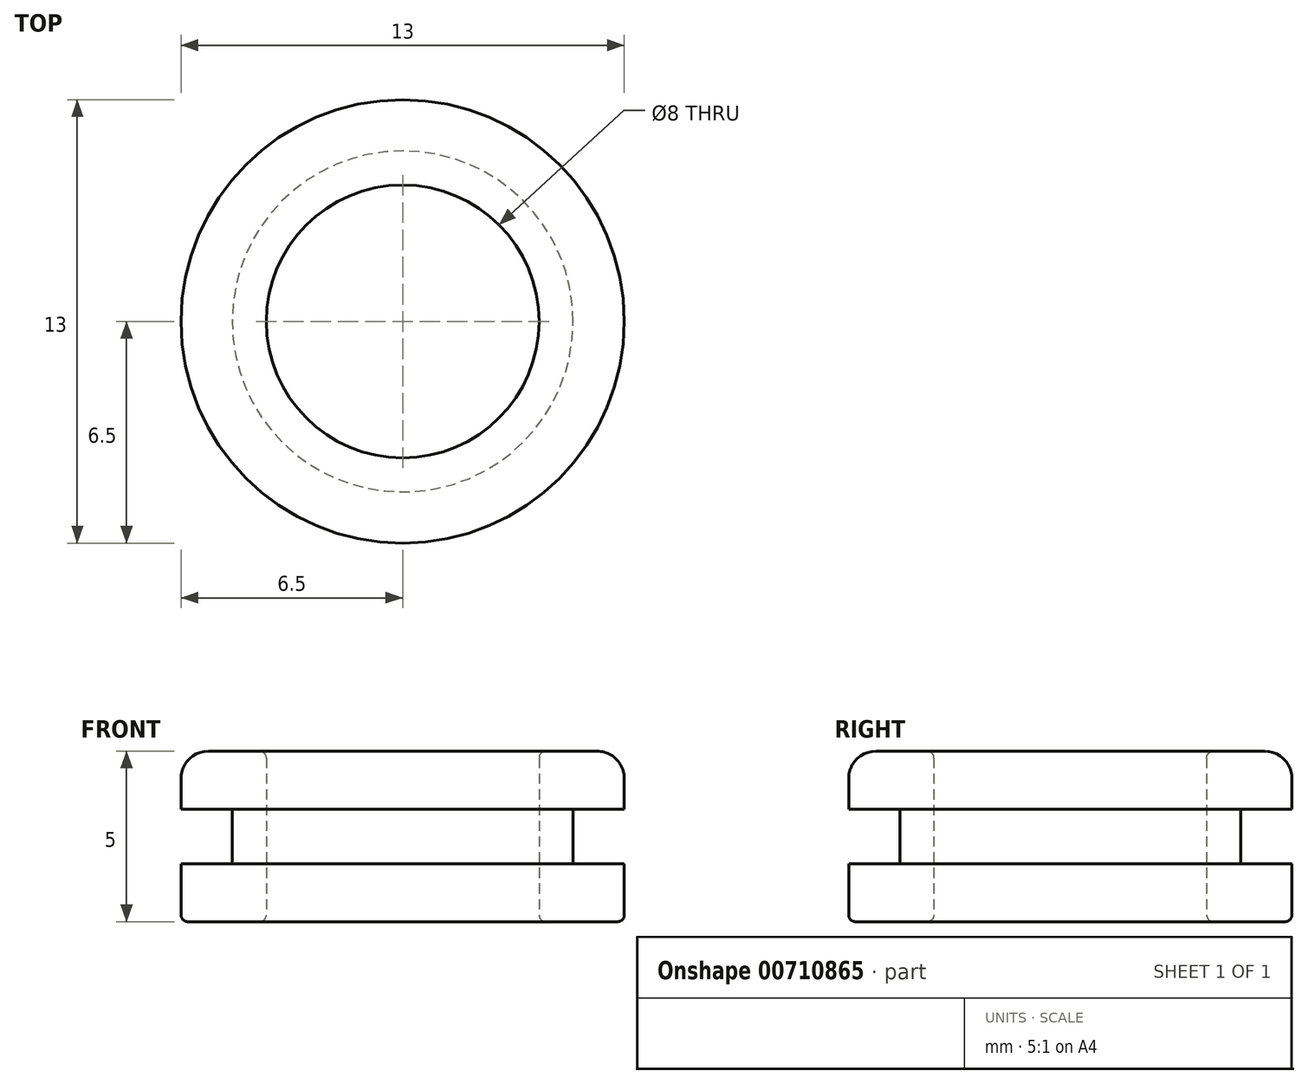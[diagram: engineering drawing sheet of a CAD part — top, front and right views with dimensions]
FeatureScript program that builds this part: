
annotation { "Feature Type Name" : "Feature", "Feature Type Description" : "" }
export const myFeature = defineFeature(function(context is Context, id is Id, definition is map)
    precondition{}
    {
        {
            var Q0;
            Q0=qCreatedBy(makeId("Front.planeOp"),FACE);
            var sketch = newSketch(context, id + "F0", { "sketchPlane" : qUnion([Q0])});
            skLineSegment(sketch, "E0", {"start": v(4, 0) * mm, "end": v(6.5, 0) * mm});
            skLineSegment(sketch, "E1", {"start": v(6.5, 0) * mm, "end": v(6.5, 1.7) * mm});
            skLineSegment(sketch, "E2", {"start": v(6.5, 1.7) * mm, "end": v(5, 1.7) * mm});
            skLineSegment(sketch, "E3", {"start": v(5, 1.7) * mm, "end": v(5, 3.3) * mm});
            skLineSegment(sketch, "E4", {"start": v(5, 3.3) * mm, "end": v(6.5, 3.3) * mm});
            skLineSegment(sketch, "E5", {"start": v(6.5, 3.3) * mm, "end": v(6.5, 5) * mm});
            skLineSegment(sketch, "E6", {"start": v(6.5, 5) * mm, "end": v(4, 5) * mm});
            skLineSegment(sketch, "E7", {"start": v(4, 5) * mm, "end": v(4, 0) * mm});
            skLineSegment(sketch, "E8", {"start": v(0, 0) * mm, "end": v(0, 7.33) * mm, "construction": true});
            skSolve(sketch);
        }
        {
            var Q0;
            Q0 = qSketchRegion(id + "F0", true);
            var Q1;
            Q1=sQuery(id+"F0.wireOp",EDGE,"E8");
            revolve(context, id + "F1", {"surfaceOperationType" : NewSurfaceOperationType.NEW, "entities" : qUnion([Q0]), "axis" : qUnion([Q1]), "revolveType" : RevolveType.FULL});
        }
        {
            var Q0;
            Q0=makeQuery(id+"F1.opRevolve","SWEPT_EDGE",EDGE,{"disambiguationData":[OSD([sQuery(id+"F0.wireOp",EDGE,"E5"),sQuery(id+"F0.wireOp",EDGE,"E6")])]});
            fillet(context, id + "F2", {"entities" : qUnion([Q0]), "radius" : 0.8 * mm, "tangentPropagation" : true, "allowEdgeOverflow" : false});
        }
        {
            var Q0;
            Q0=makeQuery(id+"F1.opRevolve","SWEPT_EDGE",EDGE,{"disambiguationData":[OSD([sQuery(id+"F0.wireOp",EDGE,"E6"),sQuery(id+"F0.wireOp",EDGE,"E7")])]});
            var Q1;
            Q1=makeQuery(id+"F1.opRevolve","SWEPT_EDGE",EDGE,{"disambiguationData":[OSD([sQuery(id+"F0.wireOp",EDGE,"E0"),sQuery(id+"F0.wireOp",EDGE,"E7")])]});
            var Q2;
            Q2=makeQuery(id+"F1.opRevolve","SWEPT_EDGE",EDGE,{"disambiguationData":[OSD([sQuery(id+"F0.wireOp",EDGE,"E0"),sQuery(id+"F0.wireOp",EDGE,"E1")])]});
            fillet(context, id + "F3", {"entities" : qUnion([Q0, Q1, Q2]), "radius" : 0.2 * mm, "tangentPropagation" : true, "allowEdgeOverflow" : false});
        }
    });
